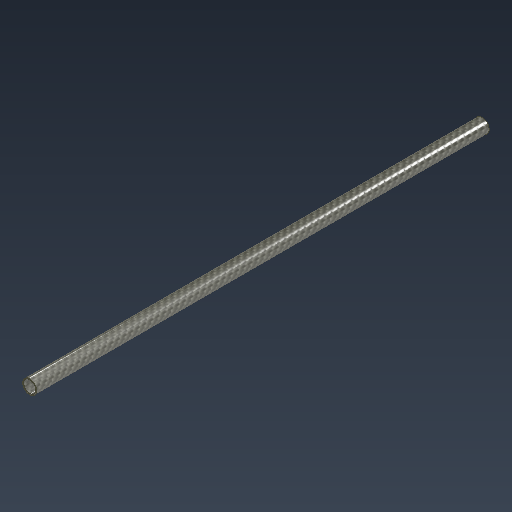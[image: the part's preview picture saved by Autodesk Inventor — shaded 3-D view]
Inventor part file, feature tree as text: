
AUTODESK INVENTOR PART (.ipt)
format: ipt  version: 2025 (Build 290162010, 162A)  size: 118,272 bytes
history: native  units: mm
features: extrude x1
ambient origin geometry x8: Origin, YZ Plane, XZ Plane, XY Plane, X Axis, Y Axis, Z Axis, Center Point
bodies: Solid1 (feature_tree)
feature tree (1):
  extrude  "Extrusion1"  Depth=16.0mm
